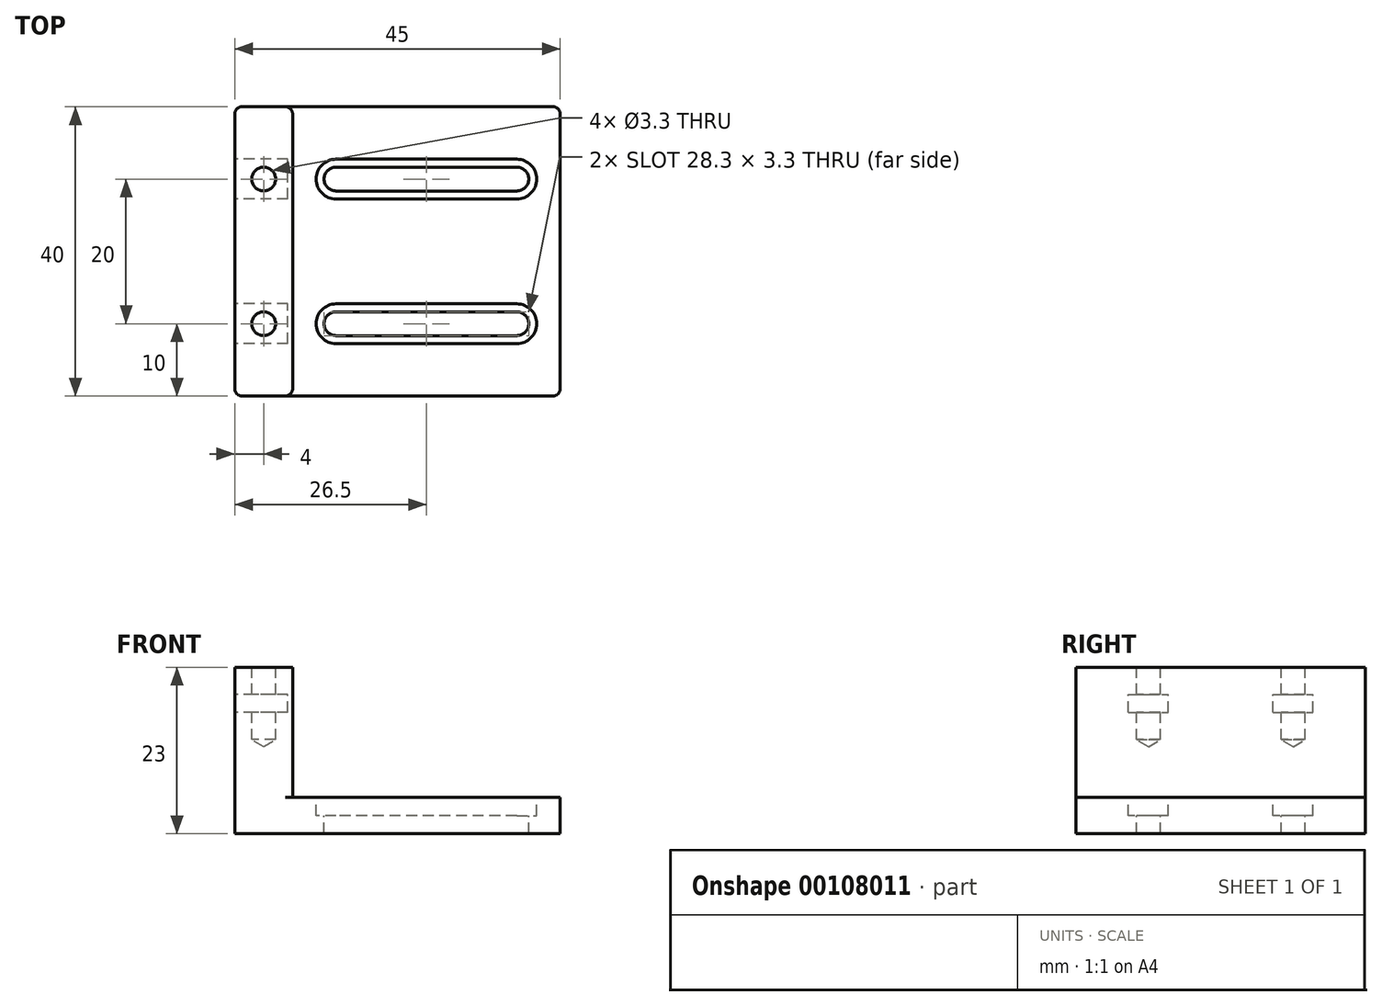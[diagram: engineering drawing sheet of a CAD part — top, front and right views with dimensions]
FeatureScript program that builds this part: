
annotation { "Feature Type Name" : "Feature", "Feature Type Description" : "" }
export const myFeature = defineFeature(function(context is Context, id is Id, definition is map)
    precondition{}
    {
        {
            var Q0;
            Q0=qCreatedBy(makeId("Front.planeOp"),FACE);
            var sketch = newSketch(context, id + "F0", { "sketchPlane" : qUnion([Q0])});
            skLineSegment(sketch, "E0.bottom", {"start": v(22.5, -2.5) * mm, "end": v(-22.5, -2.5) * mm});
            skLineSegment(sketch, "E0.top", {"start": v(22.5, 2.5) * mm, "end": v(-22.5, 2.5) * mm});
            skLineSegment(sketch, "E0.left", {"start": v(22.5, -2.5) * mm, "end": v(22.5, 2.5) * mm});
            skLineSegment(sketch, "E0.right", {"start": v(-22.5, -2.5) * mm, "end": v(-22.5, 2.5) * mm});
            skPoint(sketch, "E0.middle", {"position": v(0, 0) * mm});
            skLineSegment(sketch, "E1.bottom", {"start": v(-22.5, 2.5) * mm, "end": v(-14.5, 2.5) * mm});
            skLineSegment(sketch, "E1.top", {"start": v(-22.5, 20.5) * mm, "end": v(-14.5, 20.5) * mm});
            skLineSegment(sketch, "E1.left", {"start": v(-22.5, 2.5) * mm, "end": v(-22.5, 20.5) * mm});
            skLineSegment(sketch, "E1.right", {"start": v(-14.5, 2.5) * mm, "end": v(-14.5, 20.5) * mm});
            skSolve(sketch);
        }
        {
            var Q0;
            Q0 = qSketchRegion(id + "F0", true);
            extrude(context, id + "F1", {"entities" : qUnion([Q0]), "endBound" : BoundingType.SYMMETRIC, "depth" : 40 * mm});
        }
        {
            var Q0;
            Q0=makeQuery(id+"F1.opExtrude","CAP_EDGE",EDGE,{"disambiguationData":[OSD([sQuery(id+"F0.wireOp",EDGE,"E0.right"),sQuery(id+"F0.wireOp",EDGE,"E1.left")])],"isStart":false});
            var Q1;
            Q1=makeQuery(id+"F1.opExtrude","CAP_EDGE",EDGE,{"disambiguationData":[OSD([sQuery(id+"F0.wireOp",EDGE,"E1.right")])],"isStart":false});
            var Q2;
            Q2=makeQuery(id+"F1.opExtrude","CAP_EDGE",EDGE,{"disambiguationData":[OSD([sQuery(id+"F0.wireOp",EDGE,"E0.left")])],"isStart":false});
            var Q3;
            Q3=makeQuery(id+"F1.opExtrude","CAP_EDGE",EDGE,{"disambiguationData":[OSD([sQuery(id+"F0.wireOp",EDGE,"E0.left")])],"isStart":true});
            var Q4;
            Q4=makeQuery(id+"F1.opExtrude","CAP_EDGE",EDGE,{"disambiguationData":[OSD([sQuery(id+"F0.wireOp",EDGE,"E0.right"),sQuery(id+"F0.wireOp",EDGE,"E1.left")])],"isStart":true});
            var Q5;
            Q5=makeQuery(id+"F1.opExtrude","CAP_EDGE",EDGE,{"disambiguationData":[OSD([sQuery(id+"F0.wireOp",EDGE,"E1.right")])],"isStart":true});
            fillet(context, id + "F2", {"entities" : qUnion([Q0, Q1, Q2, Q3, Q4, Q5]), "radius" : 1 * mm, "tangentPropagation" : true, "allowEdgeOverflow" : false});
        }
        {
            var Q0;
            Q0=makeQuery(id+"F1.opExtrude","SWEPT_FACE",FACE,{"disambiguationData":[OSD([sQuery(id+"F0.wireOp",EDGE,"E0.top")])]});
            var sketch = newSketch(context, id + "F3", { "sketchPlane" : qUnion([Q0])});
            skPoint(sketch, "E2", {"position": v(4, 0) * mm});
            skPoint(sketch, "E3", {"position": v(-8.5, 10) * mm});
            skPoint(sketch, "E4", {"position": v(16.5, 10) * mm});
            skPoint(sketch, "E5", {"position": v(16.5, -10) * mm});
            skPoint(sketch, "E6", {"position": v(-8.5, -10) * mm});
            skLineSegment(sketch, "E7", {"start": v(-8.5, 10) * mm, "end": v(16.5, 10) * mm});
            skLineSegment(sketch, "E8", {"start": v(-8.5, -10) * mm, "end": v(16.5, -10) * mm});
            skArc(sketch, "E9.0.startCap", {"start": v(-8.5, 8.35) * mm, "mid": v(-10.15, 10) * mm, "end": v(-8.5, 11.65) * mm});
            skArc(sketch, "E9.0.endCap", {"start": v(16.5, 11.65) * mm, "mid": v(18.15, 10) * mm, "end": v(16.5, 8.35) * mm});
            skLineSegment(sketch, "E9.0.left", {"start": v(-8.5, 11.65) * mm, "end": v(16.5, 11.65) * mm});
            skLineSegment(sketch, "E9.0.right", {"start": v(-8.5, 8.35) * mm, "end": v(16.5, 8.35) * mm});
            skArc(sketch, "E9.1.startCap", {"start": v(-8.5, -11.65) * mm, "mid": v(-10.15, -10) * mm, "end": v(-8.5, -8.35) * mm});
            skArc(sketch, "E9.1.endCap", {"start": v(16.5, -8.35) * mm, "mid": v(18.15, -10) * mm, "end": v(16.5, -11.65) * mm});
            skLineSegment(sketch, "E9.1.left", {"start": v(-8.5, -8.35) * mm, "end": v(16.5, -8.35) * mm});
            skLineSegment(sketch, "E9.1.right", {"start": v(-8.5, -11.65) * mm, "end": v(16.5, -11.65) * mm});
            skSolve(sketch);
        }
        {
            var Q0;
            Q0 = qSketchRegion(id + "F3", true);
            extrude(context, id + "F4", {"entities" : qUnion([Q0]), "operationType" : NewBodyOperationType.REMOVE, "oppositeDirection" : true, "depth" : 5 * mm});
        }
        {
            var Q0;
            Q0=makeQuery(id+"F1.opExtrude","SWEPT_FACE",FACE,{"disambiguationData":[OSD([sQuery(id+"F0.wireOp",EDGE,"E0.top")])]});
            var sketch = newSketch(context, id + "F5", { "sketchPlane" : qUnion([Q0])});
            skPoint(sketch, "E10", {"position": v(-8.5, 10) * mm});
            skPoint(sketch, "E11", {"position": v(16.5, 10) * mm});
            skPoint(sketch, "E12", {"position": v(-8.5, -10) * mm});
            skPoint(sketch, "E13", {"position": v(16.5, -10) * mm});
            skLineSegment(sketch, "E14", {"start": v(-8.5, 10) * mm, "end": v(16.5, 10) * mm});
            skLineSegment(sketch, "E15", {"start": v(-8.5, -10) * mm, "end": v(16.5, -10) * mm});
            skArc(sketch, "E16.0.startCap", {"start": v(-8.5, 7.25) * mm, "mid": v(-11.25, 10) * mm, "end": v(-8.5, 12.75) * mm});
            skArc(sketch, "E16.0.endCap", {"start": v(16.5, 12.75) * mm, "mid": v(19.25, 10) * mm, "end": v(16.5, 7.25) * mm});
            skLineSegment(sketch, "E16.0.left", {"start": v(-8.5, 12.75) * mm, "end": v(16.5, 12.75) * mm});
            skLineSegment(sketch, "E16.0.right", {"start": v(-8.5, 7.25) * mm, "end": v(16.5, 7.25) * mm});
            skArc(sketch, "E16.1.startCap", {"start": v(-8.5, -12.75) * mm, "mid": v(-11.25, -10) * mm, "end": v(-8.5, -7.25) * mm});
            skArc(sketch, "E16.1.endCap", {"start": v(16.5, -7.25) * mm, "mid": v(19.25, -10) * mm, "end": v(16.5, -12.75) * mm});
            skLineSegment(sketch, "E16.1.left", {"start": v(-8.5, -7.25) * mm, "end": v(16.5, -7.25) * mm});
            skLineSegment(sketch, "E16.1.right", {"start": v(-8.5, -12.75) * mm, "end": v(16.5, -12.75) * mm});
            skSolve(sketch);
        }
        {
            var Q0;
            Q0 = qSketchRegion(id + "F5", true);
            extrude(context, id + "F6", {"entities" : qUnion([Q0]), "operationType" : NewBodyOperationType.REMOVE, "oppositeDirection" : true, "depth" : 2.5 * mm});
        }
        {
            var Q0;
            Q0=makeQuery(id+"F1.opExtrude","SWEPT_FACE",FACE,{"disambiguationData":[OSD([sQuery(id+"F0.wireOp",EDGE,"E1.top")])]});
            var sketch = newSketch(context, id + "F7", { "sketchPlane" : qUnion([Q0])});
            skLineSegment(sketch, "E17", {"start": v(-18.5, 0) * mm, "end": v(-18.5, 10) * mm});
            skPoint(sketch, "E18", {"position": v(-18.5, 0) * mm});
            skPoint(sketch, "E19", {"position": v(-18.5, 10) * mm});
            skLineSegment(sketch, "E20", {"start": v(-18.5, 0) * mm, "end": v(-18.5, -10) * mm});
            skPoint(sketch, "E21", {"position": v(-18.5, -10) * mm});
            skSolve(sketch);
        }
        {
            var Q0;
            Q0=sQuery(id+"F7.wireOp",VERTEX,"E19");
            var Q1;
            Q1=sQuery(id+"F7.wireOp",VERTEX,"E21");
            var Q2;
            Q2=makeQuery(id+"F1.opExtrude","SWEPT_BODY",BODY,{"disambiguationData":[OSD([sQuery(id+"F0.wireOp",EDGE,"E0.bottom"),sQuery(id+"F0.wireOp",EDGE,"E0.top"),sQuery(id+"F0.wireOp",EDGE,"E0.left"),sQuery(id+"F0.wireOp",EDGE,"E0.right"),sQuery(id+"F0.wireOp",EDGE,"E1.top"),sQuery(id+"F0.wireOp",EDGE,"E1.left"),sQuery(id+"F0.wireOp",EDGE,"E1.right")])]});
            hole(context, id + "F8", {"style" : HoleStyle.SIMPLE, "endStyle" : HoleEndStyle.BLIND, "holeDiameter" : 3.3 * mm, "holeDepth" : 10 * mm, "startFromSketch" : true, "locations" : qUnion([Q0, Q1]), "scope" : qUnion([Q2])});
        }
        {
            var Q0;
            Q0=makeQuery(id+"F1.opExtrude","SWEPT_FACE",FACE,{"disambiguationData":[OSD([sQuery(id+"F0.wireOp",EDGE,"E0.right"),sQuery(id+"F0.wireOp",EDGE,"E1.left")])]});
            var sketch = newSketch(context, id + "F9", { "sketchPlane" : qUnion([Q0])});
            skPoint(sketch, "E22", {"position": v(-10, 20.5) * mm});
            skPoint(sketch, "E23", {"position": v(10, 20.5) * mm});
            skLineSegment(sketch, "E24.bottom", {"start": v(-7.25, 14.25) * mm, "end": v(-12.75, 14.25) * mm});
            skLineSegment(sketch, "E24.top", {"start": v(-7.25, 16.75) * mm, "end": v(-12.75, 16.75) * mm});
            skLineSegment(sketch, "E24.left", {"start": v(-7.25, 14.25) * mm, "end": v(-7.25, 16.75) * mm});
            skLineSegment(sketch, "E24.right", {"start": v(-12.75, 14.25) * mm, "end": v(-12.75, 16.75) * mm});
            skPoint(sketch, "E24.middle", {"position": v(-10, 15.5) * mm});
            skPoint(sketch, "E25", {"position": v(10, 15.5) * mm});
            skLineSegment(sketch, "E26.bottom", {"start": v(12.75, 14.25) * mm, "end": v(7.25, 14.25) * mm});
            skLineSegment(sketch, "E26.top", {"start": v(12.75, 16.75) * mm, "end": v(7.25, 16.75) * mm});
            skLineSegment(sketch, "E26.left", {"start": v(12.75, 14.25) * mm, "end": v(12.75, 16.75) * mm});
            skLineSegment(sketch, "E26.right", {"start": v(7.25, 14.25) * mm, "end": v(7.25, 16.75) * mm});
            skSolve(sketch);
        }
        {
            var Q0;
            Q0 = qSketchRegion(id + "F9", true);
            extrude(context, id + "F10", {"entities" : qUnion([Q0]), "operationType" : NewBodyOperationType.REMOVE, "oppositeDirection" : true, "depth" : 7.35 * mm});
        }
    });
